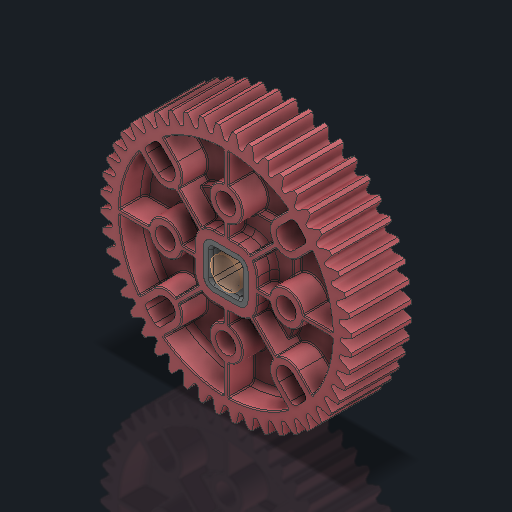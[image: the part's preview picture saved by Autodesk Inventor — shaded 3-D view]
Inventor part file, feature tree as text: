
AUTODESK INVENTOR PART (.ipt)
format: ipt  version: 2023.2 (Build 272271030, 271C)  size: 4,146,688 bytes
history: native  units: in
note: dims shown in document units (in); Inventor stores cm internally (conversion verified against a paired STEP export)
features: other x6, sketch x1
ambient origin geometry x8: Origin, YZ Plane, XZ Plane, XY Plane, X Axis, Y Axis, Z Axis, Center Point
bodies: Solid1 (feature_tree), Solid2 (feature_tree)
feature tree (7):
  other  "HS 48T Gear, No Insert.ipt"
  other  "Solid1::HS 48T Gear, No Insert.ipt"
  other  "Solid2::HS 48T Gear, No Insert.ipt"
  other  "TaggingFeature1"
  sketch  "Sketch1"  dims[d0=0.3937in]
  other  "Srf1"
  other  "Srf1::Derived"
